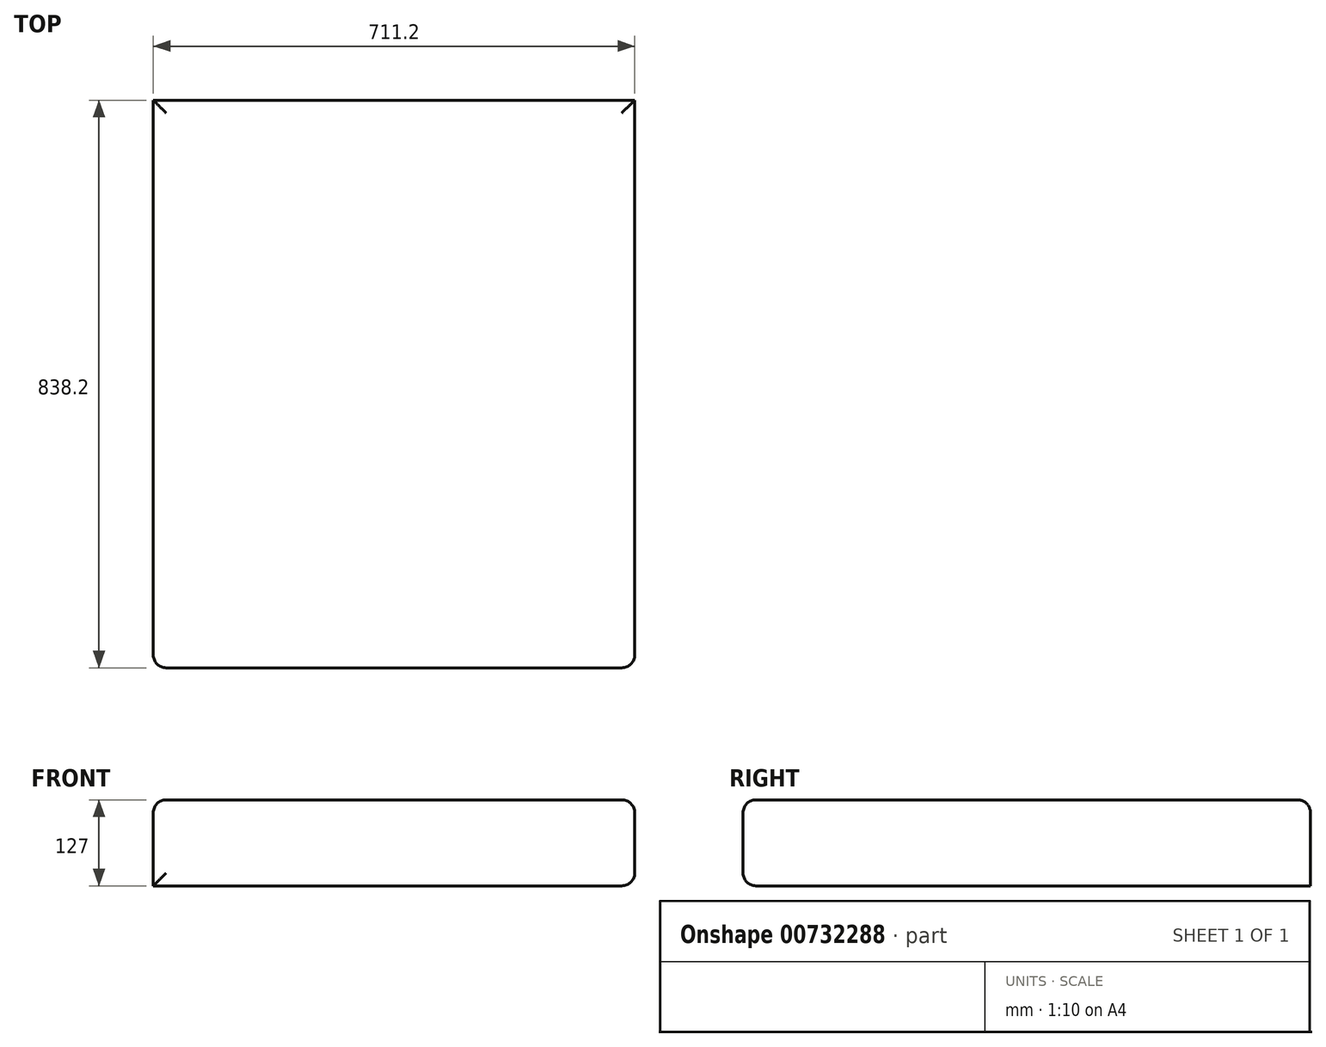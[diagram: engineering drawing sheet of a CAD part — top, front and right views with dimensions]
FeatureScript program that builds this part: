
annotation { "Feature Type Name" : "Feature", "Feature Type Description" : "" }
export const myFeature = defineFeature(function(context is Context, id is Id, definition is map)
    precondition{}
    {
        {
            var Q0;
            Q0=qCreatedBy(makeId("Top.planeOp"),FACE);
            var sketch = newSketch(context, id + "F0", { "sketchPlane" : qUnion([Q0])});
            skLineSegment(sketch, "E0.bottom", {"start": v(355.6, 419.1) * mm, "end": v(-355.6, 419.1) * mm});
            skLineSegment(sketch, "E0.top", {"start": v(355.6, -419.1) * mm, "end": v(-355.6, -419.1) * mm});
            skLineSegment(sketch, "E0.left", {"start": v(355.6, 419.1) * mm, "end": v(355.6, -419.1) * mm});
            skLineSegment(sketch, "E0.right", {"start": v(-355.6, 419.1) * mm, "end": v(-355.6, -419.1) * mm});
            skPoint(sketch, "E0.middle", {"position": v(0, 0) * mm});
            skSolve(sketch);
        }
        {
            var Q0;
            Q0 = qSketchRegion(id + "F0", true);
            extrude(context, id + "F1", {"entities" : qUnion([Q0]), "depth" : 127 * mm, "offsetDistance" : 25.4 * mm});
        }
        {
            var Q0;
            Q0=makeQuery(id+"F1.opExtrude","CAP_EDGE",EDGE,{"disambiguationData":[OSD([sQuery(id+"F0.wireOp",EDGE,"E0.right")])],"isStart":false});
            var Q1;
            Q1=makeQuery(id+"F1.opExtrude","CAP_EDGE",EDGE,{"disambiguationData":[OSD([sQuery(id+"F0.wireOp",EDGE,"E0.top")])],"isStart":false});
            var Q2;
            Q2=makeQuery(id+"F1.opExtrude","CAP_EDGE",EDGE,{"disambiguationData":[OSD([sQuery(id+"F0.wireOp",EDGE,"E0.left")])],"isStart":false});
            var Q3;
            Q3=makeQuery(id+"F1.opExtrude","CAP_EDGE",EDGE,{"disambiguationData":[OSD([sQuery(id+"F0.wireOp",EDGE,"E0.bottom")])],"isStart":false});
            var Q4;
            Q4=makeQuery(id+"F1.opExtrude","CAP_EDGE",EDGE,{"disambiguationData":[OSD([sQuery(id+"F0.wireOp",EDGE,"E0.top")])],"isStart":true});
            var Q5;
            Q5=makeQuery(id+"F1.opExtrude","SWEPT_EDGE",EDGE,{"disambiguationData":[OSD([sQuery(id+"F0.wireOp",EDGE,"E0.top"),sQuery(id+"F0.wireOp",EDGE,"E0.left")])]});
            var Q6;
            Q6=makeQuery(id+"F1.opExtrude","SWEPT_EDGE",EDGE,{"disambiguationData":[OSD([sQuery(id+"F0.wireOp",EDGE,"E0.top"),sQuery(id+"F0.wireOp",EDGE,"E0.right")])]});
            var Q7;
            Q7=makeQuery(id+"F1.opExtrude","CAP_EDGE",EDGE,{"disambiguationData":[OSD([sQuery(id+"F0.wireOp",EDGE,"E0.left")])],"isStart":true});
            fillet(context, id + "F2", {"entities" : qUnion([Q0, Q1, Q2, Q3, Q4, Q5, Q6, Q7]), "radius" : 19.05 * mm, "tangentPropagation" : true, "allowEdgeOverflow" : false});
        }
    });
